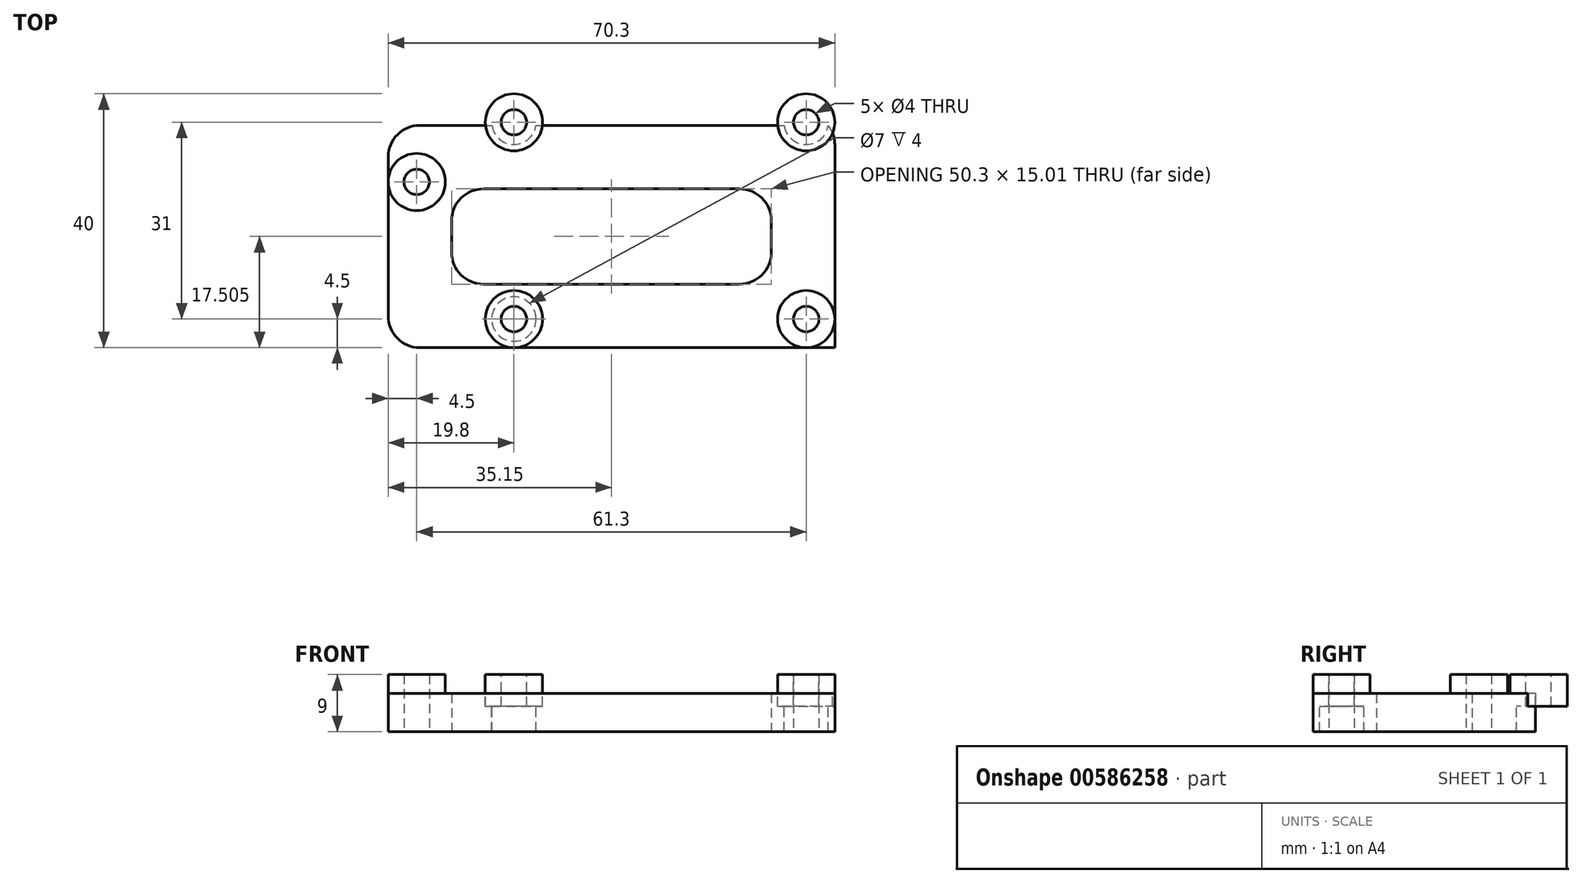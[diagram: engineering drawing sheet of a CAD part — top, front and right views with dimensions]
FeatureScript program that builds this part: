
annotation { "Feature Type Name" : "Feature", "Feature Type Description" : "" }
export const myFeature = defineFeature(function(context is Context, id is Id, definition is map)
    precondition{}
    {
        {
            assignVariable(context, id + "F0", {"name" : "circuitBottomClearing", "anyValue" : 3});
        }
        {
            assignVariable(context, id + "F1", {"name" : "fullHeight", "anyValue" : 9});
        }
        {
            assignVariable(context, id + "F2", {"name" : "baseHeight", "anyValue" : getVariable(context, 'fullHeight') - getVariable(context, 'circuitBottomClearing')});
        }
        {
            assignVariable(context, id + "F3", {"name" : "mountHeight", "anyValue" : 5});
        }
        {
            var Q0;
            Q0=qCreatedBy(makeId("Top.planeOp"),FACE);
            var sketch = newSketch(context, id + "F4", { "sketchPlane" : qUnion([Q0])});
            skLineSegment(sketch, "E0.bottom", {"start": v(-38, 15.5) * mm, "end": v(38.5, 15.5) * mm, "construction": true});
            skLineSegment(sketch, "E0.top", {"start": v(-38, -15.5) * mm, "end": v(38.5, -15.5) * mm, "construction": true});
            skLineSegment(sketch, "E0.left", {"start": v(-38, 15.5) * mm, "end": v(-38, -15.5) * mm, "construction": true});
            skLineSegment(sketch, "E0.right", {"start": v(38.5, 15.5) * mm, "end": v(38.5, -15.5) * mm, "construction": true});
            skLineSegment(sketch, "E1", {"start": v(32.9, 0) * mm, "end": v(32.9, -15.5) * mm, "construction": true});
            skLineSegment(sketch, "E2", {"start": v(38.5, -12.8) * mm, "end": v(-38, -12.8) * mm, "construction": true});
            skLineSegment(sketch, "E3", {"start": v(-38, 12.8) * mm, "end": v(38.5, 12.8) * mm, "construction": true});
            skLineSegment(sketch, "E4", {"start": v(-32.4, 15.5) * mm, "end": v(-32.4, -15.5) * mm, "construction": true});
            skCircle(sketch, "E5", {"center": v(-30.4, 10.8) * mm, "radius": 2 * mm});
            skCircle(sketch, "E6", {"center": v(30.9, -10.8) * mm, "radius": 2 * mm});
            skLineSegment(sketch, "E7", {"start": v(-38, 0) * mm, "end": v(38.5, 0) * mm, "construction": true});
            skCircle(sketch, "E8", {"center": v(-30.4, 10.8) * mm, "radius": 4.5 * mm});
            skCircle(sketch, "E9", {"center": v(30.9, -10.8) * mm, "radius": 4.5 * mm});
            skSolve(sketch);
        }
        {
            var Q0;
            Q0=qSketchRegion(id+"F4",true);
            extrude(context, id + "F5", {"entities" : qUnion([Q0]), "depth" : (getVariable(context, 'fullHeight')) * mm});
        }
        {
            var Q0;
            Q0=makeQuery(id+"F4.imprint","IMPRINT",FACE,{"disambiguationData":[TD([[makeQuery(id+"F4.imprint","IMPRINT",EDGE,{"derivedFrom":sQuery(id+"F4.wireOp",EDGE,"E5")}),-1.0]])]});
            var sketch = newSketch(context, id + "F6", { "sketchPlane" : qUnion([Q0])});
            skPoint(sketch, "E10.0", {"position": v(-30.4, 10.8) * mm});
            skPoint(sketch, "E11.0", {"position": v(30.9, -10.8) * mm});
            skPoint(sketch, "E12.bottom.start.orphan", {"position": v(31.4, -5.76) * mm});
            skPoint(sketch, "E13.start.orphan", {"position": v(34.07, 18.62) * mm});
            skPoint(sketch, "E12.top.start.orphan", {"position": v(28.62, 18.62) * mm});
            skPoint(sketch, "E14.orphan", {"position": v(-30.4, -11.11) * mm});
            skLineSegment(sketch, "E15.bottom", {"start": v(-24.9, 9.71) * mm, "end": v(25.4, 9.71) * mm});
            skLineSegment(sketch, "E15.top", {"start": v(-24.9, -5.3) * mm, "end": v(25.4, -5.3) * mm});
            skLineSegment(sketch, "E15.left", {"start": v(-24.9, 9.71) * mm, "end": v(-24.9, -5.3) * mm});
            skLineSegment(sketch, "E15.right", {"start": v(25.4, 9.71) * mm, "end": v(25.4, -5.3) * mm});
            skLineSegment(sketch, "E16.bottom", {"start": v(-34.9, 19.71) * mm, "end": v(35.4, 19.71) * mm});
            skLineSegment(sketch, "E16.top", {"start": v(-34.9, -15.3) * mm, "end": v(35.4, -15.3) * mm});
            skLineSegment(sketch, "E16.left", {"start": v(-34.9, 19.71) * mm, "end": v(-34.9, -15.3) * mm});
            skLineSegment(sketch, "E16.right", {"start": v(35.4, 19.71) * mm, "end": v(35.4, -15.3) * mm});
            skSolve(sketch);
        }
        {
            var Q0;
            Q0=qSketchRegion(id+"F6",true);
            extrude(context, id + "F7", {"entities" : qUnion([Q0]), "operationType" : NewBodyOperationType.ADD, "depth" : (getVariable(context, 'baseHeight')) * mm});
        }
        {
            var Q0;
            Q0=makeQuery(id+"F5.opExtrude","CAP_FACE",FACE,{"disambiguationData":[OSD([sQuery(id+"F4.wireOp",EDGE,"E5"),sQuery(id+"F4.wireOp",EDGE,"E8")])],"isStart":false});
            var sketch = newSketch(context, id + "F8", { "sketchPlane" : qUnion([Q0])});
            skCircle(sketch, "E17", {"center": v(-15.1, -10.8) * mm, "radius": 2 * mm});
            skCircle(sketch, "E18", {"center": v(-15.1, -10.8) * mm, "radius": 4.5 * mm});
            skCircle(sketch, "E19", {"center": v(-15.1, 20.2) * mm, "radius": 2 * mm});
            skCircle(sketch, "E20", {"center": v(-15.1, 20.2) * mm, "radius": 4.5 * mm});
            skCircle(sketch, "E21", {"center": v(30.9, 20.2) * mm, "radius": 2 * mm});
            skCircle(sketch, "E22", {"center": v(30.9, 20.2) * mm, "radius": 4.5 * mm});
            skPoint(sketch, "E23.0", {"position": v(30.9, -10.8) * mm});
            skLineSegment(sketch, "E24.0", {"start": v(38.5, -12.8) * mm, "end": v(-38, -12.8) * mm});
            skLineSegment(sketch, "E25.0", {"start": v(32.9, 0) * mm, "end": v(32.9, -15.5) * mm});
            skLineSegment(sketch, "E26", {"start": v(30.9, -10.8) * mm, "end": v(-38.76, -10.8) * mm, "construction": true});
            skLineSegment(sketch, "E27", {"start": v(-15.1, -10.8) * mm, "end": v(-15.1, 18.3) * mm, "construction": true});
            skLineSegment(sketch, "E28", {"start": v(30.9, -10.8) * mm, "end": v(30.9, 20.43) * mm, "construction": true});
            skSolve(sketch);
        }
        {
            var Q0;
            Q0=qSketchRegion(id+"F8",true);
            extrude(context, id + "F9", {"entities" : qUnion([Q0]), "operationType" : NewBodyOperationType.ADD, "oppositeDirection" : true, "depth" : (getVariable(context, 'mountHeight')) * mm});
        }
        {
            var Q0;
            Q0=makeQuery(id+"F9.boolean.opBoolean","MERGE",FACE,{"derivedFrom":[makeQuery(id+"F5.opExtrude","CAP_FACE",FACE,{"disambiguationData":[OSD([sQuery(id+"F4.wireOp",EDGE,"E6"),sQuery(id+"F4.wireOp",EDGE,"E9")])],"isStart":false}),makeQuery(id+"F9.opExtrude","CAP_FACE",FACE,{"disambiguationData":[OSD([sQuery(id+"F8.wireOp",EDGE,"6bb8e593-27b5-4253-ada7-62b1f03044dc.0"),sQuery(id+"F8.wireOp",EDGE,"E24.0"),sQuery(id+"F8.wireOp",EDGE,"E25.0")])],"isStart":true})]});
            var sketch = newSketch(context, id + "F10", { "sketchPlane" : qUnion([Q0])});
            skPoint(sketch, "E29.0", {"position": v(30.9, -10.8) * mm});
            skCircle(sketch, "E30", {"center": v(30.9, -10.8) * mm, "radius": 2 * mm});
            skPoint(sketch, "E31.0", {"position": v(-30.4, 10.8) * mm});
            skCircle(sketch, "E32", {"center": v(-30.4, 10.8) * mm, "radius": 2 * mm});
            skSolve(sketch);
        }
        {
            var Q0;
            Q0=qSketchRegion(id+"F10",true);
            extrude(context, id + "F11", {"entities" : qUnion([Q0]), "operationType" : NewBodyOperationType.REMOVE, "endBound" : BoundingType.THROUGH_ALL, "oppositeDirection" : true, "depth" : 9 * mm});
        }
        {
            var Q0;
            Q0=makeQuery(id+"F9.opExtrude","CAP_FACE",FACE,{"disambiguationData":[OSD([sQuery(id+"F8.wireOp",EDGE,"E19"),sQuery(id+"F8.wireOp",EDGE,"E20")])],"isStart":true});
            var sketch = newSketch(context, id + "F12", { "sketchPlane" : qUnion([Q0])});
            skCircle(sketch, "E33.0", {"center": v(-15.1, 20.2) * mm, "radius": 2 * mm});
            skCircle(sketch, "E34.0", {"center": v(30.9, 20.2) * mm, "radius": 2 * mm});
            skCircle(sketch, "E35.0", {"center": v(-15.1, -10.8) * mm, "radius": 2 * mm});
            skCircle(sketch, "E36", {"center": v(-15.1, 20.2) * mm, "radius": 3.5 * mm});
            skCircle(sketch, "E37", {"center": v(30.9, 20.2) * mm, "radius": 3.5 * mm});
            skCircle(sketch, "E38", {"center": v(-15.1, -10.8) * mm, "radius": 3.5 * mm});
            skSolve(sketch);
        }
        {
            var Q0;
            Q0=qSketchRegion(id+"F12",true);
            extrude(context, id + "F13", {"entities" : qUnion([Q0]), "operationType" : NewBodyOperationType.REMOVE, "oppositeDirection" : true, "depth" : 28 * mm, "hasSecondDirection" : true, "secondDirectionOppositeDirection" : true, "secondDirectionDepth" : (getVariable(context, 'mountHeight')) * mm});
        }
        {
            var Q0;
            Q0=makeQuery(id+"F9.opExtrude","CAP_FACE",FACE,{"disambiguationData":[OSD([sQuery(id+"F8.wireOp",EDGE,"E19"),sQuery(id+"F8.wireOp",EDGE,"E20")])],"isStart":true});
            var sketch = newSketch(context, id + "F14", { "sketchPlane" : qUnion([Q0])});
            skCircle(sketch, "E39.0", {"center": v(-15.1, 20.2) * mm, "radius": 2 * mm});
            skCircle(sketch, "E40.0", {"center": v(30.9, 20.2) * mm, "radius": 2 * mm});
            skCircle(sketch, "E41.0", {"center": v(-15.1, -10.8) * mm, "radius": 2 * mm});
            skCircle(sketch, "E42.0", {"center": v(30.9, -10.8) * mm, "radius": 2 * mm});
            skSolve(sketch);
        }
        {
            var Q0;
            Q0=qSketchRegion(id+"F14",true);
            extrude(context, id + "F15", {"entities" : qUnion([Q0]), "operationType" : NewBodyOperationType.REMOVE, "endBound" : BoundingType.THROUGH_ALL, "oppositeDirection" : true, "depth" : 25 * mm});
        }
        {
            var Q0;
            Q0=makeQuery(id+"F7.opExtrude","SWEPT_EDGE",EDGE,{"disambiguationData":[OSD([sQuery(id+"F6.wireOp",EDGE,"E16.top"),sQuery(id+"F6.wireOp",EDGE,"E16.left")])]});
            var Q1;
            Q1=makeQuery(id+"F7.opExtrude","SWEPT_EDGE",EDGE,{"disambiguationData":[OSD([sQuery(id+"F6.wireOp",EDGE,"E15.top"),sQuery(id+"F6.wireOp",EDGE,"E15.right")])]});
            var Q2;
            Q2=makeQuery(id+"F7.opExtrude","SWEPT_EDGE",EDGE,{"disambiguationData":[OSD([sQuery(id+"F6.wireOp",EDGE,"E15.top"),sQuery(id+"F6.wireOp",EDGE,"E15.left")])]});
            var Q3;
            Q3=makeQuery(id+"F7.opExtrude","SWEPT_EDGE",EDGE,{"disambiguationData":[OSD([sQuery(id+"F6.wireOp",EDGE,"E16.bottom"),sQuery(id+"F6.wireOp",EDGE,"E16.left")])]});
            var Q4;
            Q4=makeQuery(id+"F7.opExtrude","SWEPT_EDGE",EDGE,{"disambiguationData":[OSD([sQuery(id+"F6.wireOp",EDGE,"E15.bottom"),sQuery(id+"F6.wireOp",EDGE,"E15.left")])]});
            var Q5;
            Q5=makeQuery(id+"F7.opExtrude","SWEPT_EDGE",EDGE,{"disambiguationData":[OSD([sQuery(id+"F6.wireOp",EDGE,"E15.bottom"),sQuery(id+"F6.wireOp",EDGE,"E15.right")])]});
            var Q6;
            Q6=makeQuery(id+"F7.opExtrude","SWEPT_EDGE",EDGE,{"disambiguationData":[OSD([sQuery(id+"F6.wireOp",EDGE,"E16.bottom"),sQuery(id+"F6.wireOp",EDGE,"E16.right")])]});
            fillet(context, id + "F16", {"entities" : qUnion([Q0, Q1, Q2, Q3, Q4, Q5, Q6]), "radius" : 5 * mm, "tangentPropagation" : true, "allowEdgeOverflow" : false});
        }
    });
